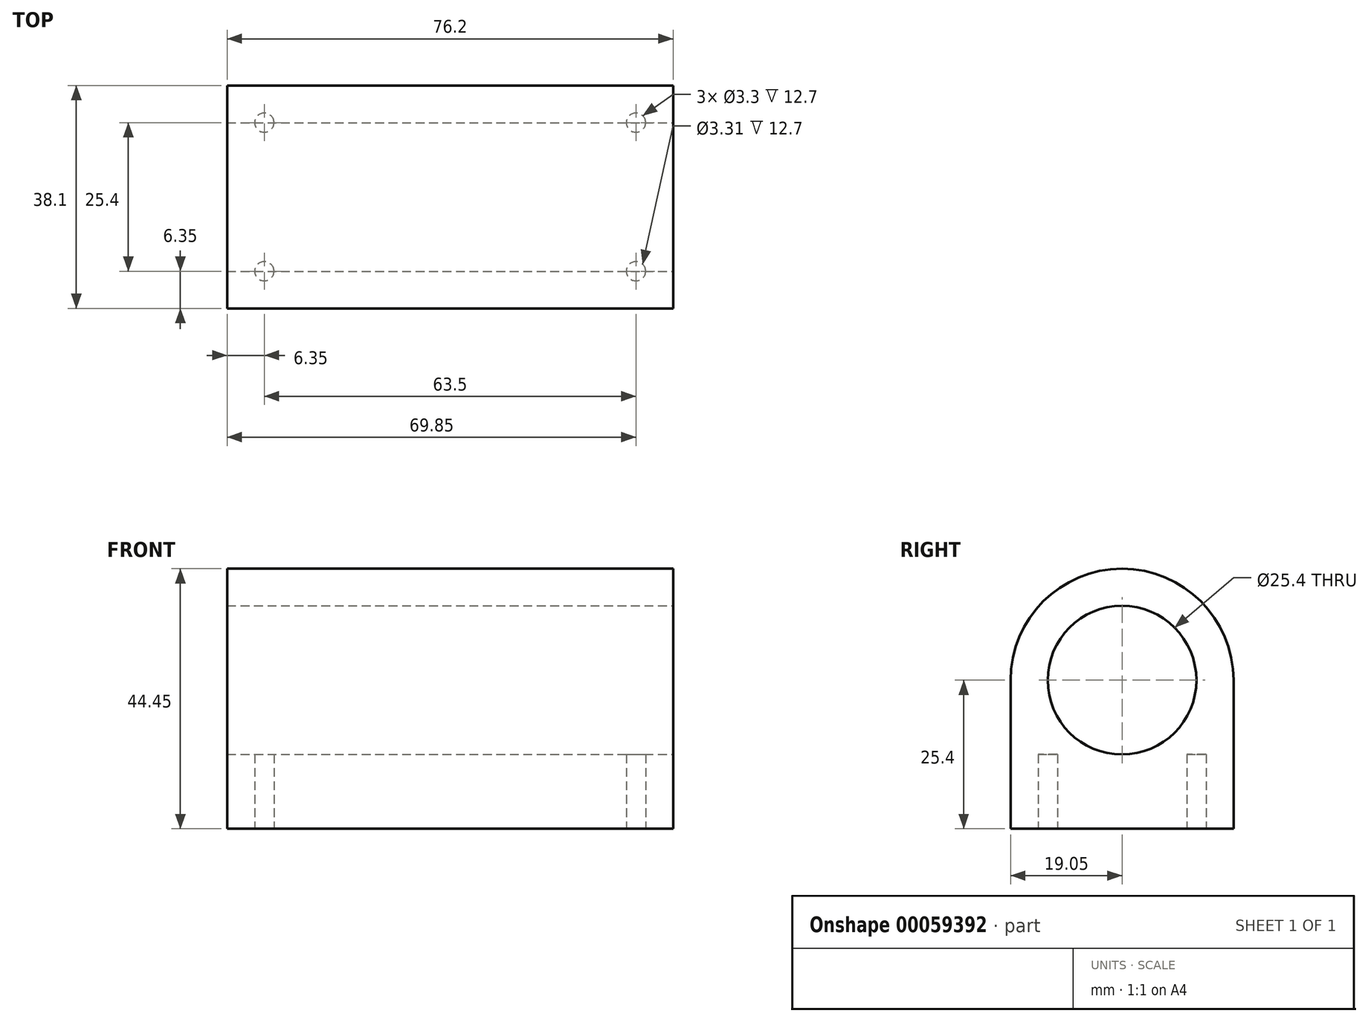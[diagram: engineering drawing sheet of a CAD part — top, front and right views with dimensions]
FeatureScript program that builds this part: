
annotation { "Feature Type Name" : "Feature", "Feature Type Description" : "" }
export const myFeature = defineFeature(function(context is Context, id is Id, definition is map)
    precondition{}
    {
        {
            var Q0;
            Q0=qCreatedBy(makeId("Right.planeOp"),FACE);
            var sketch = newSketch(context, id + "F0", { "sketchPlane" : qUnion([Q0])});
            skArc(sketch, "E0", {"start": v(19.05, 0) * mm, "mid": v(0, 19.05) * mm, "end": v(-19.05, 0) * mm});
            skLineSegment(sketch, "E1", {"start": v(-19.05, 0) * mm, "end": v(-19.05, -25.4) * mm});
            skLineSegment(sketch, "E2", {"start": v(19.05, 0) * mm, "end": v(19.05, -25.4) * mm});
            skLineSegment(sketch, "E3", {"start": v(-19.05, -25.4) * mm, "end": v(19.05, -25.4) * mm});
            skCircle(sketch, "E4", {"center": v(0, 0) * mm, "radius": 12.7 * mm});
            skSolve(sketch);
        }
        {
            var Q0;
            Q0 = qSketchRegion(id + "F0", true);
            extrude(context, id + "F1", {"entities" : qUnion([Q0]), "oppositeDirection" : true, "depth" : 76.2 * mm});
        }
        {
            var Q0;
            Q0=makeQuery(id+"F1.opExtrude","SWEPT_FACE",FACE,{"disambiguationData":[OSD([sQuery(id+"F0.wireOp",EDGE,"E3")])]});
            var sketch = newSketch(context, id + "F2", { "sketchPlane" : qUnion([Q0])});
            skCircle(sketch, "E5", {"center": v(-69.85, 12.7) * mm, "radius": 1.65 * mm});
            skCircle(sketch, "E6", {"center": v(-6.35, 12.7) * mm, "radius": 1.65 * mm});
            skCircle(sketch, "E7", {"center": v(-6.35, -12.7) * mm, "radius": 1.65 * mm});
            skCircle(sketch, "E8", {"center": v(-69.85, -12.7) * mm, "radius": 1.65 * mm});
            skSolve(sketch);
        }
        {
            var Q0;
            Q0 = qSketchRegion(id + "F2", true);
            extrude(context, id + "F3", {"entities" : qUnion([Q0]), "operationType" : NewBodyOperationType.REMOVE, "oppositeDirection" : true, "depth" : 12.7 * mm});
        }
    });
